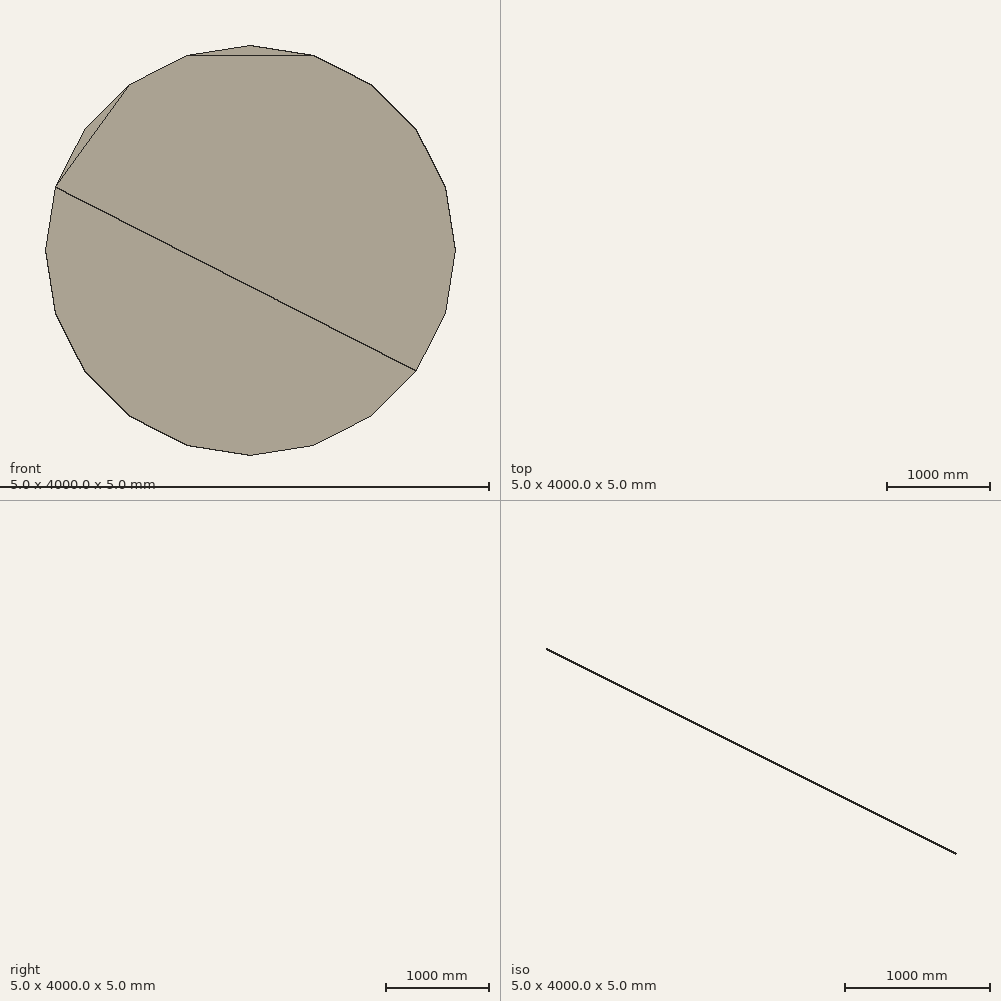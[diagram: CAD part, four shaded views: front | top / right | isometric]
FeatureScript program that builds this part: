
annotation { "Feature Type Name" : "Feature", "Feature Type Description" : "" }
export const myFeature = defineFeature(function(context is Context, id is Id, definition is map)
    precondition{}
    {
        {
            var Q0;
            Q0=qCreatedBy(makeId("Front.planeOp"),FACE);
            var sketch = newSketch(context, id + "F0", { "sketchPlane" : qUnion([Q0])});
            skCircle(sketch, "E0", {"center": v(0, 0) * mm, "radius": 2.5 * mm});
            skSolve(sketch);
        }
        {
            var Q0;
            Q0=qSketchRegion(id+"F0",true);
            extrude(context, id + "F1", {"entities" : qUnion([Q0]), "depth" : 4000 * mm, "offsetDistance" : 25 * mm});
        }
    });
